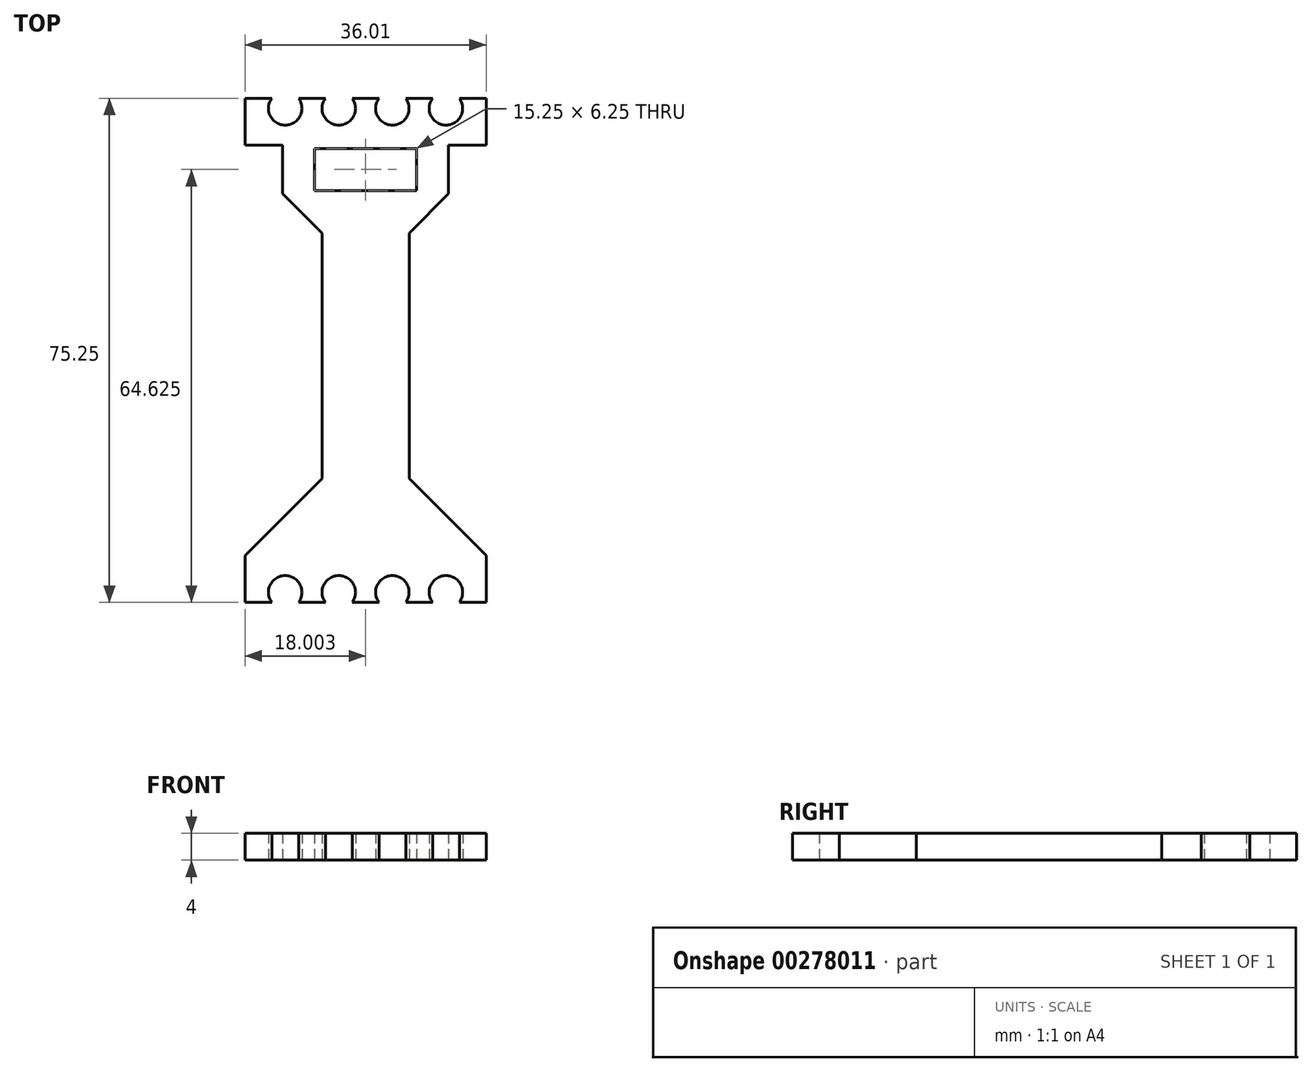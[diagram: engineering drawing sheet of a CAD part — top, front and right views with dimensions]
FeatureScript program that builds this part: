
annotation { "Feature Type Name" : "Feature", "Feature Type Description" : "" }
export const myFeature = defineFeature(function(context is Context, id is Id, definition is map)
    precondition{}
    {
        {
            var Q0;
            Q0=qCreatedBy(makeId("Top.planeOp"),FACE);
            var sketch = newSketch(context, id + "F0", { "sketchPlane" : qUnion([Q0])});
            skArc(sketch, "E0", {"start": v(4, 7) * mm, "mid": v(6, 3) * mm, "end": v(8, 7) * mm});
            skArc(sketch, "E1", {"start": v(12, 7) * mm, "mid": v(14, 3) * mm, "end": v(16, 7) * mm});
            skArc(sketch, "E2", {"start": v(20, 7) * mm, "mid": v(22, 3) * mm, "end": v(24, 7) * mm});
            skArc(sketch, "E3", {"start": v(28, 7) * mm, "mid": v(30, 3) * mm, "end": v(32, 7) * mm});
            skLineSegment(sketch, "E4", {"start": v(4, 7) * mm, "end": v(0, 7) * mm});
            skLineSegment(sketch, "E5", {"start": v(0, 7) * mm, "end": v(0, 0) * mm});
            skLineSegment(sketch, "E6", {"start": v(36, 0) * mm, "end": v(36, 7) * mm});
            skLineSegment(sketch, "E7", {"start": v(36, 7) * mm, "end": v(32, 7) * mm});
            skLineSegment(sketch, "E8", {"start": v(6, 5.5) * mm, "end": v(3.5, 5.5) * mm, "construction": true});
            skLineSegment(sketch, "E9", {"start": v(6, 5.5) * mm, "end": v(4, 7) * mm, "construction": true});
            skLineSegment(sketch, "E10", {"start": v(28, 7) * mm, "end": v(24, 7) * mm});
            skLineSegment(sketch, "E11", {"start": v(20, 7) * mm, "end": v(16, 7) * mm});
            skLineSegment(sketch, "E12", {"start": v(12, 7) * mm, "end": v(8, 7) * mm});
            skLineSegment(sketch, "E13", {"start": v(8.5, 5.5) * mm, "end": v(11.5, 5.5) * mm, "construction": true});
            skLineSegment(sketch, "E14", {"start": v(6, 3) * mm, "end": v(6, 0) * mm, "construction": true});
            skLineSegment(sketch, "E15", {"start": v(30.4, 0) * mm, "end": v(30.4, -7.25) * mm});
            skLineSegment(sketch, "E16", {"start": v(5.6, -7.25) * mm, "end": v(5.6, 0) * mm});
            skLineSegment(sketch, "E17.bottom", {"start": v(10.38, -0.5) * mm, "end": v(25.63, -0.5) * mm});
            skLineSegment(sketch, "E17.top", {"start": v(10.38, -6.75) * mm, "end": v(25.63, -6.75) * mm});
            skLineSegment(sketch, "E17.left", {"start": v(10.38, -0.5) * mm, "end": v(10.38, -6.75) * mm});
            skLineSegment(sketch, "E17.right", {"start": v(25.63, -0.5) * mm, "end": v(25.63, -6.75) * mm});
            skPoint(sketch, "E18", {"position": v(18, -0.5) * mm});
            skPoint(sketch, "E19", {"position": v(30.4, -3.62) * mm});
            skPoint(sketch, "E20", {"position": v(25.63, -3.62) * mm});
            skPoint(sketch, "E21", {"position": v(18, 7) * mm});
            skLineSegment(sketch, "E22", {"start": v(0, 0) * mm, "end": v(5.6, 0) * mm});
            skLineSegment(sketch, "E23", {"start": v(36, 0) * mm, "end": v(30.4, 0) * mm});
            skLineSegment(sketch, "E24", {"start": v(10.38, -0.5) * mm, "end": v(5.6, -0.5) * mm, "construction": true});
            skLineSegment(sketch, "E25", {"start": v(25.63, -0.5) * mm, "end": v(30.4, -0.5) * mm, "construction": true});
            skLineSegment(sketch, "E26", {"start": v(-30.1, -30.62) * mm, "end": v(67.3, -30.62) * mm, "construction": true});
            skLineSegment(sketch, "E27.MirrorCS", {"start": v(8.5, -66.75) * mm, "end": v(11.5, -66.75) * mm, "construction": true});
            skLineSegment(sketch, "E28.MirrorCS", {"start": v(6, -66.75) * mm, "end": v(3.5, -66.75) * mm, "construction": true});
            skLineSegment(sketch, "E29.MirrorCS", {"start": v(6, -66.75) * mm, "end": v(4, -68.25) * mm, "construction": true});
            skLineSegment(sketch, "E30.MirrorCS", {"start": v(20, -68.25) * mm, "end": v(16, -68.25) * mm});
            skArc(sketch, "E31.MirrorCS", {"start": v(20, -68.25) * mm, "mid": v(22, -64.25) * mm, "end": v(24, -68.25) * mm});
            skArc(sketch, "E32.MirrorCS", {"start": v(12, -68.25) * mm, "mid": v(14, -64.25) * mm, "end": v(16, -68.25) * mm});
            skPoint(sketch, "E33.MirrorP", {"position": v(18, -68.25) * mm});
            skLineSegment(sketch, "E34.MirrorCS", {"start": v(36, -61.25) * mm, "end": v(36, -68.25) * mm});
            skLineSegment(sketch, "E35.MirrorCS", {"start": v(28, -68.25) * mm, "end": v(24, -68.25) * mm});
            skArc(sketch, "E36.MirrorCS", {"start": v(28, -68.25) * mm, "mid": v(30, -64.25) * mm, "end": v(32, -68.25) * mm});
            skArc(sketch, "E37.MirrorCS", {"start": v(4, -68.25) * mm, "mid": v(6, -64.25) * mm, "end": v(8, -68.25) * mm});
            skLineSegment(sketch, "E38.MirrorCS", {"start": v(4, -68.25) * mm, "end": v(0, -68.25) * mm});
            skLineSegment(sketch, "E39.MirrorCS", {"start": v(36, -68.25) * mm, "end": v(32, -68.25) * mm});
            skLineSegment(sketch, "E40.MirrorCS", {"start": v(0, -68.25) * mm, "end": v(0, -61.25) * mm});
            skLineSegment(sketch, "E41.MirrorCS", {"start": v(12, -68.25) * mm, "end": v(8, -68.25) * mm});
            skLineSegment(sketch, "E42", {"start": v(5.6, -7.25) * mm, "end": v(11.5, -13.15) * mm});
            skLineSegment(sketch, "E43", {"start": v(11.5, -13.15) * mm, "end": v(11.5, -49.75) * mm});
            skLineSegment(sketch, "E44", {"start": v(11.5, -49.75) * mm, "end": v(0, -61.25) * mm});
            skLineSegment(sketch, "E45", {"start": v(36, -61.25) * mm, "end": v(24.5, -49.75) * mm});
            skLineSegment(sketch, "E46", {"start": v(24.5, -49.75) * mm, "end": v(24.5, -13.15) * mm});
            skLineSegment(sketch, "E47", {"start": v(24.5, -13.15) * mm, "end": v(30.4, -7.25) * mm});
            skSolve(sketch);
        }
        {
            var Q0;
            Q0=qSketchRegion(id+"F0",true);
            extrude(context, id + "F1", {"entities" : qUnion([Q0]), "depth" : 4 * mm});
        }
    });
